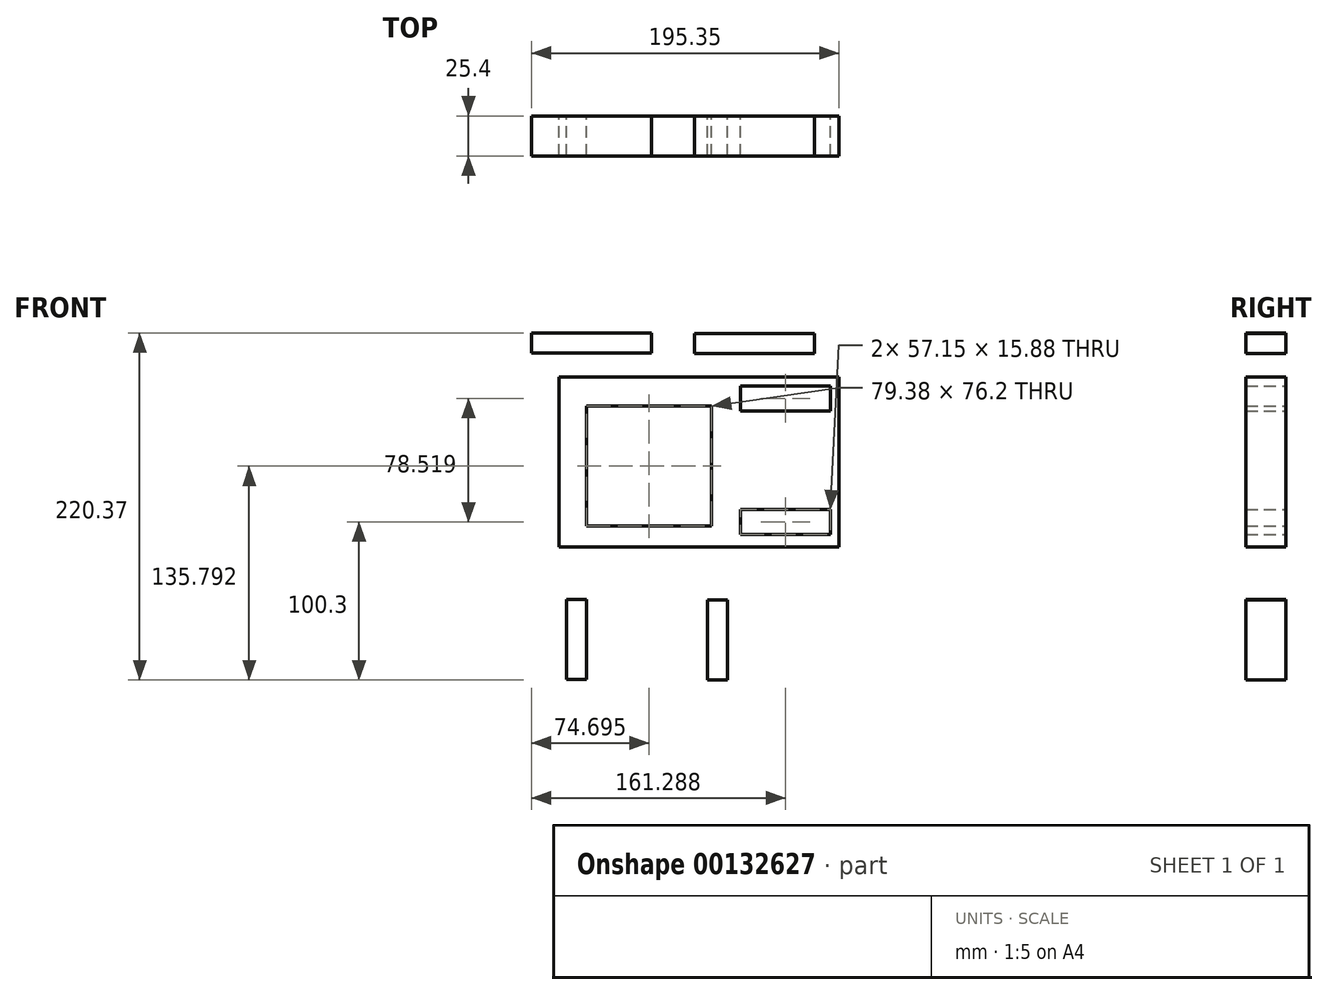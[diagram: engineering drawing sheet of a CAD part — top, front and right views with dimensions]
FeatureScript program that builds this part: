
annotation { "Feature Type Name" : "Feature", "Feature Type Description" : "" }
export const myFeature = defineFeature(function(context is Context, id is Id, definition is map)
    precondition{}
    {
        {
            var Q0;
            Q0=qCreatedBy(makeId("Front.planeOp"),FACE);
            var sketch = newSketch(context, id + "F0", { "sketchPlane" : qUnion([Q0])});
            skLineSegment(sketch, "E0.bottom", {"start": v(-61.68, 79.26) * mm, "end": v(116.12, 79.26) * mm});
            skLineSegment(sketch, "E0.top", {"start": v(-61.68, -28.69) * mm, "end": v(116.12, -28.69) * mm});
            skLineSegment(sketch, "E0.left", {"start": v(-61.68, 79.26) * mm, "end": v(-61.68, -28.69) * mm});
            skLineSegment(sketch, "E0.right", {"start": v(116.12, 79.26) * mm, "end": v(116.12, -28.69) * mm});
            skLineSegment(sketch, "E1.bottom", {"start": v(53.48, -4.8) * mm, "end": v(110.63, -4.8) * mm});
            skLineSegment(sketch, "E1.top", {"start": v(53.48, -20.67) * mm, "end": v(110.63, -20.67) * mm});
            skLineSegment(sketch, "E1.left", {"start": v(53.48, -4.8) * mm, "end": v(53.48, -20.67) * mm});
            skLineSegment(sketch, "E1.right", {"start": v(110.63, -4.8) * mm, "end": v(110.63, -20.67) * mm});
            skLineSegment(sketch, "E2.bottom", {"start": v(53.48, 73.73) * mm, "end": v(110.63, 73.73) * mm});
            skLineSegment(sketch, "E2.top", {"start": v(53.48, 57.85) * mm, "end": v(110.63, 57.85) * mm});
            skLineSegment(sketch, "E2.left", {"start": v(53.48, 73.73) * mm, "end": v(53.48, 57.85) * mm});
            skLineSegment(sketch, "E2.right", {"start": v(110.63, 73.73) * mm, "end": v(110.63, 57.85) * mm});
            skLineSegment(sketch, "E3.bottom", {"start": v(-44.22, -15.34) * mm, "end": v(35.15, -15.34) * mm});
            skLineSegment(sketch, "E3.top", {"start": v(-44.22, 60.86) * mm, "end": v(35.15, 60.86) * mm});
            skLineSegment(sketch, "E3.left", {"start": v(-44.22, -15.34) * mm, "end": v(-44.22, 60.86) * mm});
            skLineSegment(sketch, "E3.right", {"start": v(35.15, -15.34) * mm, "end": v(35.15, 60.86) * mm});
            skSolve(sketch);
        }
        {
            var Q0;
            Q0=qCreatedBy(makeId("Front.planeOp"),FACE);
            var sketch = newSketch(context, id + "F1", { "sketchPlane" : qUnion([Q0])});
            skLineSegment(sketch, "E4.bottom", {"start": v(-79.23, 107.34) * mm, "end": v(-3.03, 107.34) * mm});
            skLineSegment(sketch, "E4.top", {"start": v(-79.23, 94.64) * mm, "end": v(-3.03, 94.64) * mm});
            skLineSegment(sketch, "E4.left", {"start": v(-79.23, 107.34) * mm, "end": v(-79.23, 94.64) * mm});
            skLineSegment(sketch, "E4.right", {"start": v(-3.03, 107.34) * mm, "end": v(-3.03, 94.64) * mm});
            skLineSegment(sketch, "E5.bottom", {"start": v(24.18, 106.92) * mm, "end": v(100.38, 106.92) * mm});
            skLineSegment(sketch, "E5.top", {"start": v(24.18, 94.22) * mm, "end": v(100.38, 94.22) * mm});
            skLineSegment(sketch, "E5.left", {"start": v(24.18, 106.92) * mm, "end": v(24.18, 94.22) * mm});
            skLineSegment(sketch, "E5.right", {"start": v(100.38, 106.92) * mm, "end": v(100.38, 94.22) * mm});
            skLineSegment(sketch, "E6.bottom", {"start": v(-57.04, -61.8) * mm, "end": v(-44.34, -61.8) * mm});
            skLineSegment(sketch, "E6.top", {"start": v(-57.04, -112.6) * mm, "end": v(-44.34, -112.6) * mm});
            skLineSegment(sketch, "E6.left", {"start": v(-57.04, -61.8) * mm, "end": v(-57.04, -112.6) * mm});
            skLineSegment(sketch, "E6.right", {"start": v(-44.34, -61.8) * mm, "end": v(-44.34, -112.6) * mm});
            skLineSegment(sketch, "E7.bottom", {"start": v(32.56, -62.23) * mm, "end": v(45.26, -62.23) * mm});
            skLineSegment(sketch, "E7.top", {"start": v(32.56, -113.03) * mm, "end": v(45.26, -113.03) * mm});
            skLineSegment(sketch, "E7.left", {"start": v(32.56, -62.23) * mm, "end": v(32.56, -113.03) * mm});
            skLineSegment(sketch, "E7.right", {"start": v(45.26, -62.23) * mm, "end": v(45.26, -113.03) * mm});
            skSolve(sketch);
        }
        {
            var Q0;
            Q0 = qSketchRegion(id + "F1", true);
            var Q1;
            Q1=makeQuery(id+"F0.imprint","IMPRINT",FACE,{"disambiguationData":[TD([[makeQuery(id+"F0.imprint","IMPRINT",EDGE,{"derivedFrom":sQuery(id+"F0.wireOp",EDGE,"E0.bottom")}),-1.0]])]});
            extrude(context, id + "F2", {"entities" : qUnion([Q0, Q1]), "depth" : 25.4 * mm});
        }
    });
